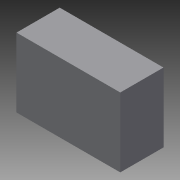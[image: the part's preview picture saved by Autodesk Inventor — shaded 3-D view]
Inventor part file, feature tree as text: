
AUTODESK INVENTOR PART (.ipt)
format: ipt  version: 2015 SP1 (Build 190203100, 203)  size: 68,608 bytes
history: native  units: mm
features: extrude x1, sketch x1
ambient origin geometry x8: Origin, YZ Plane, XZ Plane, XY Plane, X Axis, Y Axis, Z Axis, Center Point
bodies: Solid1 (feature_tree)
feature tree (2):
  extrude  "Extrusion1"  Depth=100.0mm
  sketch  "Sketch1"  dims[d0=240.0mm d1=100.0mm d2=160.0mm d3=0.0mm]
